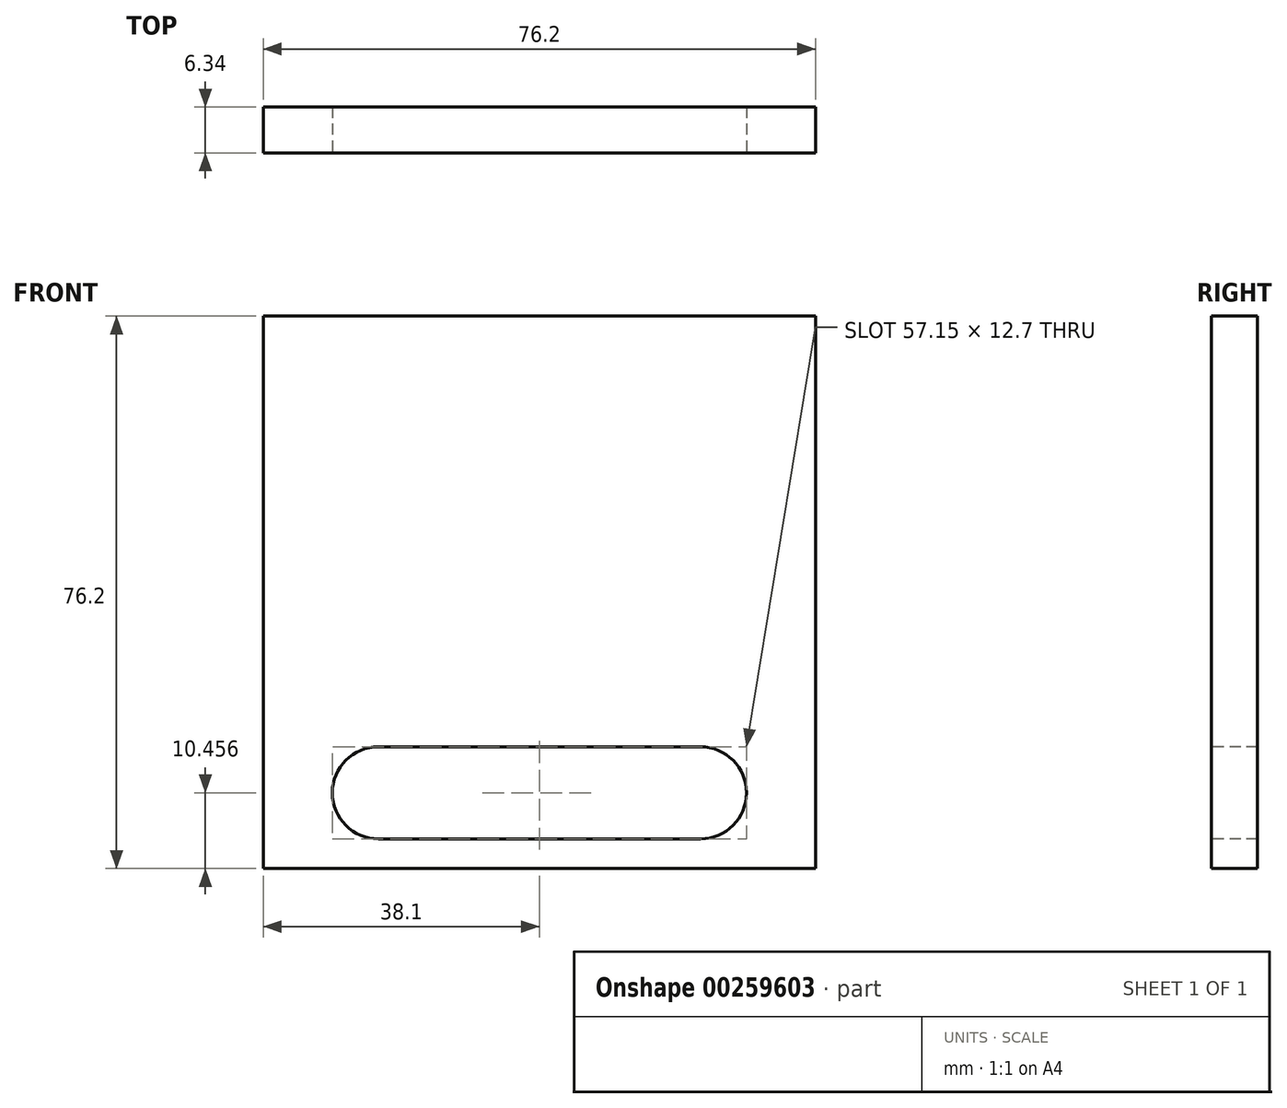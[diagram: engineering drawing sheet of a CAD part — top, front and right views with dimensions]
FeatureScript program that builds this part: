
annotation { "Feature Type Name" : "Feature", "Feature Type Description" : "" }
export const myFeature = defineFeature(function(context is Context, id is Id, definition is map)
    precondition{}
    {
        {
            var Q0;
            Q0=qCreatedBy(makeId("Front.planeOp"),FACE);
            var sketch = newSketch(context, id + "F0", { "sketchPlane" : qUnion([Q0])});
            skLineSegment(sketch, "E0.bottom", {"start": v(38.1, 0) * mm, "end": v(-38.1, 0) * mm});
            skLineSegment(sketch, "E0.top", {"start": v(38.1, 76.2) * mm, "end": v(-38.1, 76.2) * mm});
            skLineSegment(sketch, "E0.left", {"start": v(38.1, 0) * mm, "end": v(38.1, 76.2) * mm});
            skLineSegment(sketch, "E0.right", {"start": v(-38.1, 0) * mm, "end": v(-38.1, 76.2) * mm});
            skSolve(sketch);
        }
        {
            var Q0;
            Q0=makeQuery(id+"F0.imprint","IMPRINT",FACE,{"disambiguationData":[TD([[makeQuery(id+"F0.imprint","IMPRINT",EDGE,{"derivedFrom":sQuery(id+"F0.wireOp",EDGE,"E0.bottom")}),-1.0]])]});
            extrude(context, id + "F1", {"entities" : qUnion([Q0]), "depth" : 6.35 * mm, "symmetric" : true});
        }
        {
            var Q0;
            Q0=makeQuery(id+"F1.opExtrude","CAP_FACE",FACE,{"disambiguationData":[OSD([sQuery(id+"F0.wireOp",EDGE,"E0.bottom"),sQuery(id+"F0.wireOp",EDGE,"E0.top"),sQuery(id+"F0.wireOp",EDGE,"E0.left"),sQuery(id+"F0.wireOp",EDGE,"E0.right")])],"isStart":false});
            var sketch = newSketch(context, id + "F2", { "sketchPlane" : qUnion([Q0])});
            skLineSegment(sketch, "E1.bottom", {"start": v(22.23, 16.8) * mm, "end": v(-22.23, 16.8) * mm});
            skLineSegment(sketch, "E1.top", {"start": v(22.23, 4.1) * mm, "end": v(-22.23, 4.1) * mm});
            skLineSegment(sketch, "E1.left", {"start": v(22.23, 16.8) * mm, "end": v(22.23, 4.1) * mm});
            skLineSegment(sketch, "E1.right", {"start": v(-22.23, 16.8) * mm, "end": v(-22.23, 4.1) * mm});
            skPoint(sketch, "E1.middle", {"position": v(0, 10.46) * mm});
            skArc(sketch, "E2", {"start": v(-22.23, 16.8) * mm, "mid": v(-28.58, 10.46) * mm, "end": v(-22.23, 4.1) * mm});
            skArc(sketch, "E3", {"start": v(22.23, 4.1) * mm, "mid": v(28.58, 10.46) * mm, "end": v(22.23, 16.8) * mm});
            skSolve(sketch);
        }
        {
            var Q0;
            Q0=makeQuery(id+"F2.imprint","IMPRINT",FACE,{"disambiguationData":[TD([[makeQuery(id+"F2.imprint","IMPRINT",EDGE,{"derivedFrom":sQuery(id+"F2.wireOp",EDGE,"E1.right")}),-1.0]])]});
            var Q1;
            Q1=makeQuery(id+"F2.imprint","IMPRINT",FACE,{"disambiguationData":[TD([[makeQuery(id+"F2.imprint","IMPRINT",EDGE,{"derivedFrom":sQuery(id+"F2.wireOp",EDGE,"E1.bottom")}),1.0]])]});
            var Q2;
            Q2=makeQuery(id+"F2.imprint","IMPRINT",FACE,{"disambiguationData":[TD([[makeQuery(id+"F2.imprint","IMPRINT",EDGE,{"derivedFrom":sQuery(id+"F2.wireOp",EDGE,"E1.left")}),1.0]])]});
            extrude(context, id + "F3", {"entities" : qUnion([Q0, Q1, Q2]), "operationType" : NewBodyOperationType.REMOVE, "oppositeDirection" : true, "depth" : 6.35 * mm});
        }
    });
